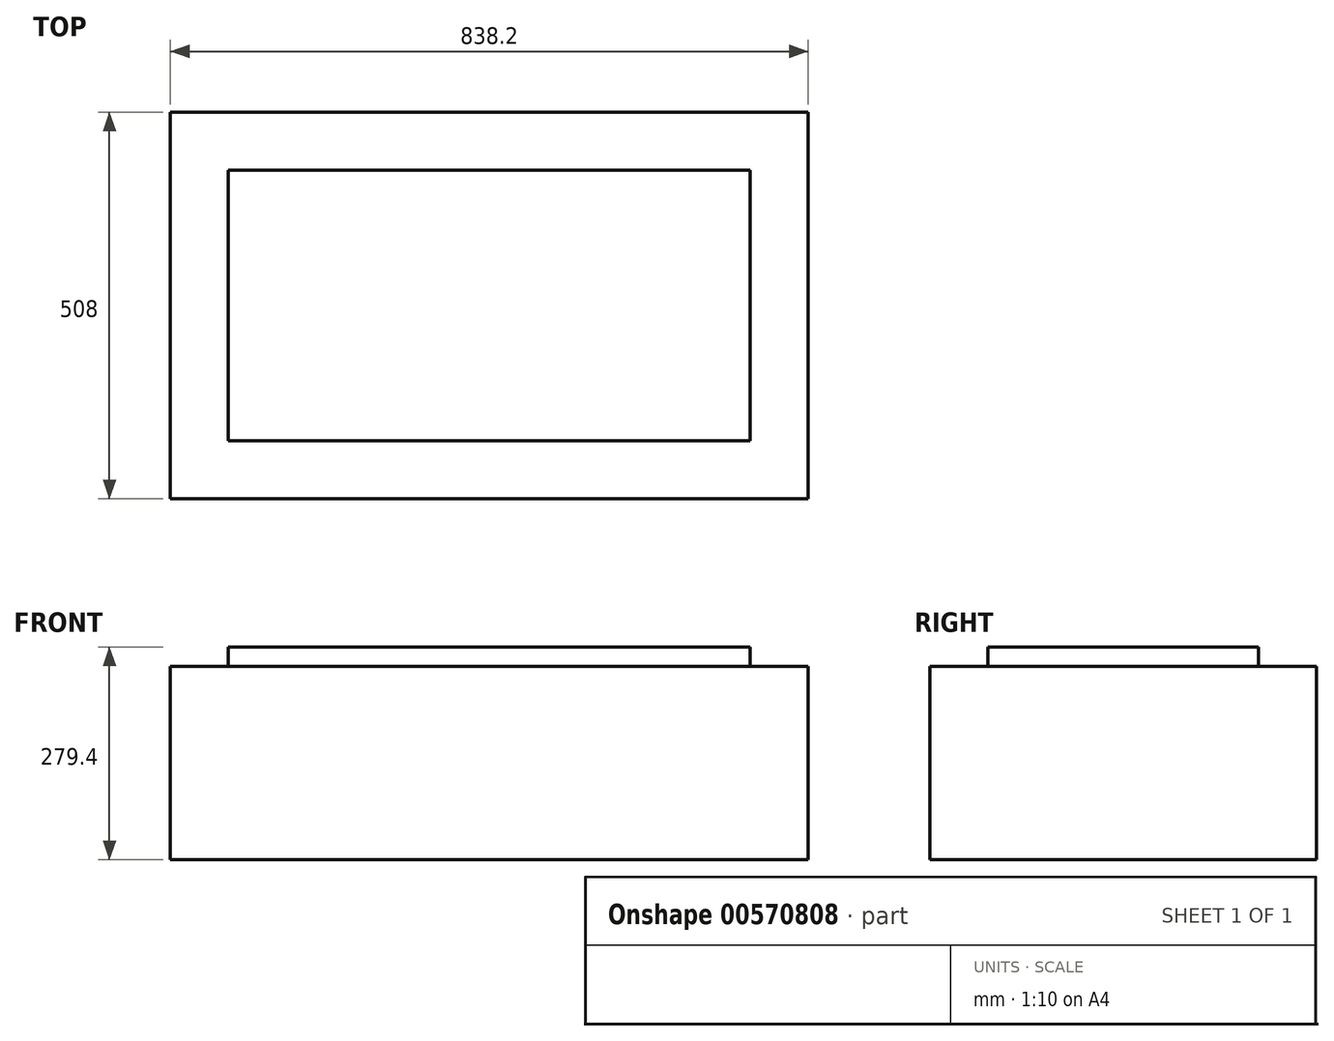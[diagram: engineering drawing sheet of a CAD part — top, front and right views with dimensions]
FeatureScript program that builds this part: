
annotation { "Feature Type Name" : "Feature", "Feature Type Description" : "" }
export const myFeature = defineFeature(function(context is Context, id is Id, definition is map)
    precondition{}
    {
        {
            var Q0;
            Q0=qCreatedBy(makeId("Top.planeOp"),FACE);
            var sketch = newSketch(context, id + "F0", { "sketchPlane" : qUnion([Q0])});
            skLineSegment(sketch, "E0.bottom", {"start": v(-678.59, 372.17) * mm, "end": v(159.61, 372.17) * mm});
            skLineSegment(sketch, "E0.top", {"start": v(-678.59, -135.83) * mm, "end": v(159.61, -135.83) * mm});
            skLineSegment(sketch, "E0.left", {"start": v(-678.59, 372.17) * mm, "end": v(-678.59, -135.83) * mm});
            skLineSegment(sketch, "E0.right", {"start": v(159.61, 372.17) * mm, "end": v(159.61, -135.83) * mm});
            skLineSegment(sketch, "E1.bottom", {"start": v(83.41, -59.63) * mm, "end": v(-602.39, -59.63) * mm});
            skLineSegment(sketch, "E1.top", {"start": v(83.41, 295.97) * mm, "end": v(-602.39, 295.97) * mm});
            skLineSegment(sketch, "E1.left", {"start": v(83.41, -59.63) * mm, "end": v(83.41, 295.97) * mm});
            skLineSegment(sketch, "E1.right", {"start": v(-602.39, -59.63) * mm, "end": v(-602.39, 295.97) * mm});
            skSolve(sketch);
        }
        {
            var Q0;
            Q0=makeQuery(id+"F0.imprint","IMPRINT",FACE,{"disambiguationData":[TD([[makeQuery(id+"F0.imprint","IMPRINT",EDGE,{"derivedFrom":sQuery(id+"F0.wireOp",EDGE,"E1.bottom")}),-1.0]])]});
            var Q1;
            Q1=makeQuery(id+"F0.imprint","IMPRINT",FACE,{"disambiguationData":[TD([[makeQuery(id+"F0.imprint","IMPRINT",EDGE,{"derivedFrom":sQuery(id+"F0.wireOp",EDGE,"E0.bottom")}),-1.0]])]});
            extrude(context, id + "F1", {"entities" : qUnion([Q0, Q1]), "depth" : 254 * mm, "offsetDistance" : 25.4 * mm});
        }
        {
            var Q0;
            Q0=makeQuery(id+"F0.imprint","IMPRINT",FACE,{"disambiguationData":[TD([[makeQuery(id+"F0.imprint","IMPRINT",EDGE,{"derivedFrom":sQuery(id+"F0.wireOp",EDGE,"E1.bottom")}),-1.0]])]});
            extrude(context, id + "F2", {"entities" : qUnion([Q0]), "operationType" : NewBodyOperationType.ADD, "depth" : 279.4 * mm, "offsetDistance" : 25.4 * mm});
        }
        {
            var Q0;
            Q0=makeQuery(id+"F1.opExtrude","CAP_FACE",FACE,{"disambiguationData":[OSD([sQuery(id+"F0.wireOp",EDGE,"E0.bottom"),sQuery(id+"F0.wireOp",EDGE,"E0.top"),sQuery(id+"F0.wireOp",EDGE,"E0.left"),sQuery(id+"F0.wireOp",EDGE,"E0.right")])],"isStart":true});
            shell(context, id + "F3", {"entities" : qUnion([Q0]), "thickness" : 0.25 * mm});
        }
    });
